# Revit family: ORSAY
name_source: partatom
category: Осветительные приборы
revit_build: Autodesk Revit 2016 (Build: 20150220_1215(x64)
units: mm (PartAtom-declared; Revit-internal decimal feet)

## family parameters
Источник света = Да
Общий = Нет
Основа = Грань
При загрузке вырезать с полостями = Нет
Размер круглого соединителя = Использовать диаметр
Тип детали = Нормальный
Точка расчета площади = Нет

## types (3) — shared parameters
ADSK_Единица измерения = Шт.
ADSK_Завод-изготовитель = ООО МГК Световые технологии
ADSK_Количество фаз = 1
ADSK_Количество фаз числовое = 1
ADSK_Коэффициент мощности = 0.92
ADSK_Масса = 0.9
ADSK_Наименование = Настенный светильник отраженного света, создающий диффузное освещение. Корпус изготовлен из экструдированного алюминия, окрашенного белой матовой краской
ADSK_Напряжение = 230 В
ADSK_Номинальная мощность = 0 кВт
ADSK_Полная мощность = 0 кВ·А
ADSK_Размер_Высота = 70 мм
ADSK_Размер_Глубина = 93 мм
ADSK_Размер_Ширина = 300 мм
ADSK_Ток = 0 А
ADSK_Энергоэффективность = 145 лм/Вт
IP Class = IP20
URL = http://www.ltcompany.com
Блок аварийного питания = Нет
Видимая форма излучения при визуализации = Нет
Группа модели = Светильники
Изготовитель = ООО МГК Световые технологии
Излучение по длине прямоугольника = 300 мм
Излучение по ширине прямоугольника = 70 мм
Класс Защиты = I
Климатическая зона = УХЛ4
Код по классификатору = D5020200
Корпус = Корпус белый пластик
Область использования = Гостиницы, Индивидуальные дома, Культурно-развлекательные, Магазины/Бутики, Объекты бытового обслуживания, Объекты общественного питания, Офисы, ТРЦ
Описание = Настенный светильник отраженного света, создающий диффузное освещение. Корпус изготовлен из экструдированного алюминия, окрашенного белой матовой краской
Плафон = <По категории>
Полная установленная мощность = 0 кВ·А
Разработчик = ООО ПРОРУБИМ
Разработчик (телефон) = +7 (495) 649-85-43
Светофильтр = 16777215
Смещение цветовой температуры при затухании лампы = <Нет>
Тип ИС = LED
Тип ПРА = Драйвер
Тип продукции = Светильник
Угол наклона = 180.00°
Файл фотометрической сетки = ORSAY.IES
zero-valued in all types: Отметка по умолчанию

## per-type parameters (varying)
| type | ADSK_Код изделия |
| ORSAY 3000K AL | 1561000020 |
| ORSAY 3000K BL/GL | 1561000030 |
| ORSAY 3000K WH | 1561000010 |

## geometry (parser evidence)
native form markers: Blend x2
no freeform markers — native parametric forms only
